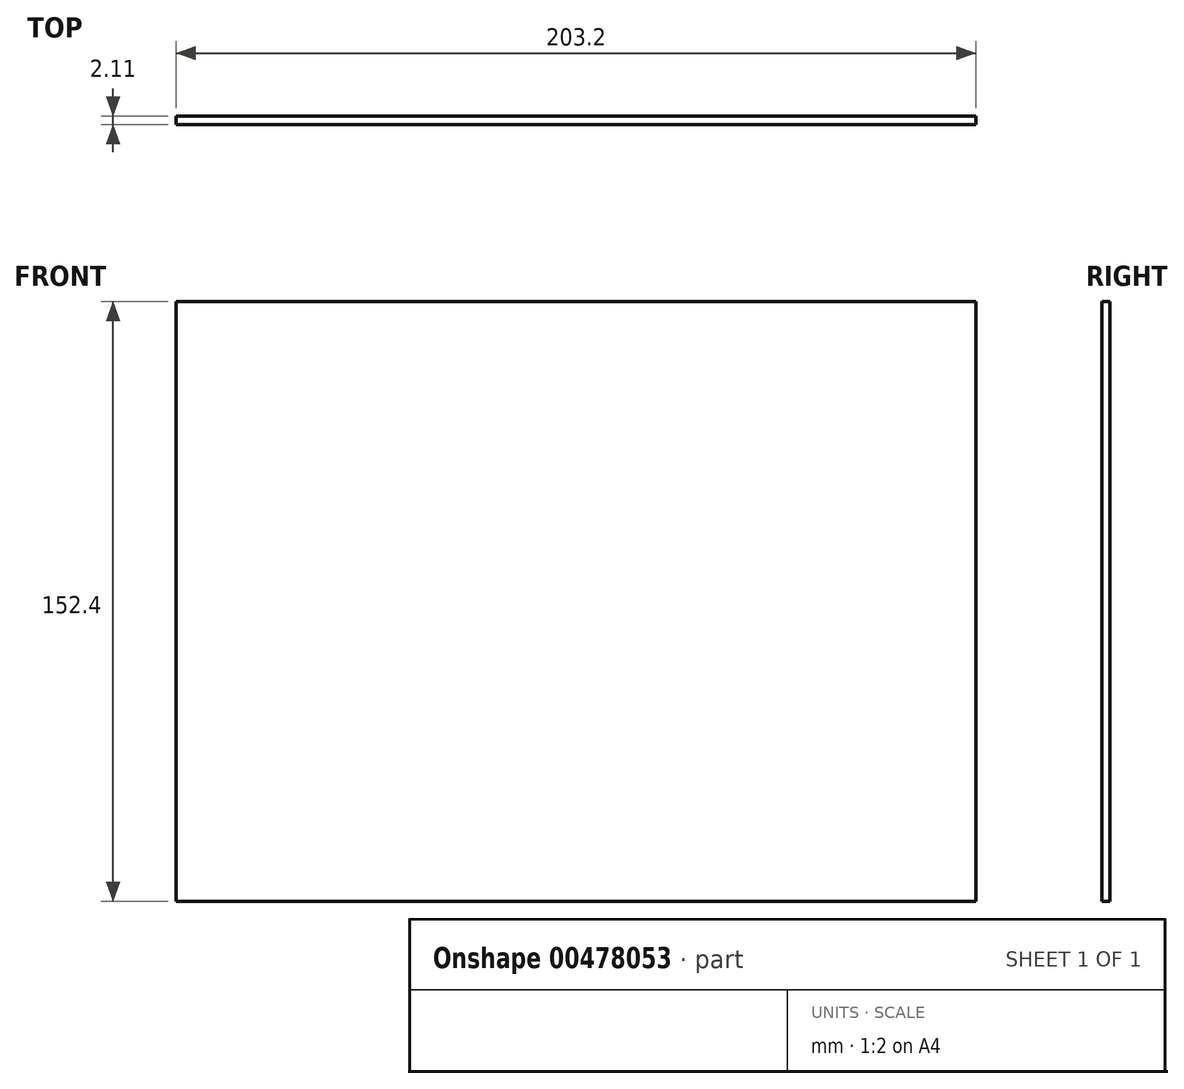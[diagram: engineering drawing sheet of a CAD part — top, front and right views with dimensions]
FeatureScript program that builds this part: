
annotation { "Feature Type Name" : "Feature", "Feature Type Description" : "" }
export const myFeature = defineFeature(function(context is Context, id is Id, definition is map)
    precondition{}
    {
        {
            var Q0;
            Q0=qCreatedBy(makeId("Front.planeOp"),FACE);
            var sketch = newSketch(context, id + "F0", { "sketchPlane" : qUnion([Q0])});
            skLineSegment(sketch, "E0.bottom", {"start": v(-145.83, 95.4) * mm, "end": v(57.37, 95.4) * mm});
            skLineSegment(sketch, "E0.top", {"start": v(-145.83, -57) * mm, "end": v(57.37, -57) * mm});
            skLineSegment(sketch, "E0.left", {"start": v(-145.83, 95.4) * mm, "end": v(-145.83, -57) * mm});
            skLineSegment(sketch, "E0.right", {"start": v(57.37, 95.4) * mm, "end": v(57.37, -57) * mm});
            skSolve(sketch);
        }
        {
            var Q0;
            Q0=qSketchRegion(id+"F0",true);
            extrude(context, id + "F1", {"entities" : qUnion([Q0]), "depth" : 2.1 * mm});
        }
    });
